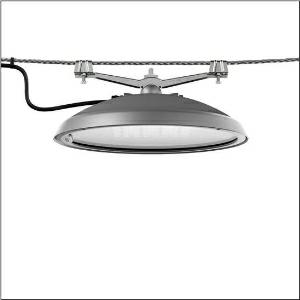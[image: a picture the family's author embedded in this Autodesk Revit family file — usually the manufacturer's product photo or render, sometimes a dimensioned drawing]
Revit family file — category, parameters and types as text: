
# Revit family: dl_r__50_iq_mini___st1_0s_5xa248w21f08ge_9981
name_source: partatom
category: Lighting Fixtures
units: mm (PartAtom-declared; Revit-internal decimal feet)

## family parameters
Cut with Voids When Loaded = No
Host = Face
Light Source = No
Part Type = Normal
Room Calculation Point = No
Round Connector Dimension = Use Diameter
Shared = No

## types (1)
- --- (1 x LED, 4580 lm, 35.2 W, 2200K)
    Apparent Load = 35 VA
    CIE Flux Codes = 37 72 97 100 100
    Color Rendering = 70
    Color Temperature = 2200K
    Default Elevation = 1800 mm
    Description = DL® 50 iQ mini, catenary luminaire, primary light control with lens, of PMMA, primary optical cover: cover, of toughened safety glass, transparent, light distribution: ST1.0s, light emission: direct distribution, primary light characteristic: symmetric, installation type: suspended mounting, LED, High Power LED, rated luminous flux: 4.580lm, luminous efficacy: 130lm/W, light colour: 722, colour temperature: 2200K, control gear: iQ Street-Remote, control: optimised constant luminous flux control (CLO 2.0), Desk-Remote (wireless, voltage-free reading and setting of iQ features in the workshop via application-optimized NFC function/RFID function), Light-Fading, Smart-Wire, Night-Set, Lumen-Switch, Temp-Guard, Auto-Match, Street-Remote, mains connection: 230..240V, AC, 50/60Hz, start of lifetime: 35W, end of service life: 36W, reduction: 17W, luminaire housing, of diecast aluminium, powder-coated, Siteco® metallic grey (DB 702S), diameter: 500mm, height: 115mm, mounting height: 4..12m, protection rating (complete): IP66, insulation class (complete): insulation class II (safety insulation), certification: CE, ENEC, ENEC+, VDE, impact resistance: IK08, permissible operating ambient temperature for outdoor applications: -25..+40°C, standard-compliant lighting for roads and squares, packaging unit: 1 piece

Light Distribution: ST1.0s
    Height = 124 mm  [stored 0.406824 ft]
    Lamp = 1 x LED
    Lamp Light Flux = 4580 lm
    Lamp Power = 35.2 W
    Lamp count = 1
    Length = 500 mm
    Luminous efficacy = 130 lm/W
    Manufacturer = Siteco
    ModVariant = No
    Model = 5XA248W21F08GE
    Number of Poles = 1
    OnlyDefault = Yes
    Power Factor = 1
    Product Name = DL® 50 iQ mini | ST1.0s
    Product group = catenary luminaire
    ProductGroupID = 6300
    Protection Class = Protection class II
    Protection Degree = IP 66
    RLX_Detail_Level = 1
    RLX_Emergency_Light_Flux = 0 lm
    RLX_Emergency_Type = 0
    RLX_Emergency_Type_DB = No
    RlxData = <blob elided: 124145 chars, md5=b6a0861d>
    Socket = socket
    Standby Power = 0 W
    System Light Flux = 4580 lm
    System Power = 35 W
    Type Comments = factory setting: luminous flux: 100 % | dim-lin: 254 | 365 mA
    Type Image = l_1242791.jpg
    URL = http://relux.com
    VarID = @adj_162385
    Voltage = 0 V
    Weight = 0.00 kg
    Width = 0 mm  [stored 0 ft]

note: [stored X ft] marks values corroborated as IEEE doubles in the binary element streams (Revit-internal decimal feet)

## geometry (parser evidence)
native form markers: Blend x4, Sweep x13
no freeform markers — native parametric forms only
